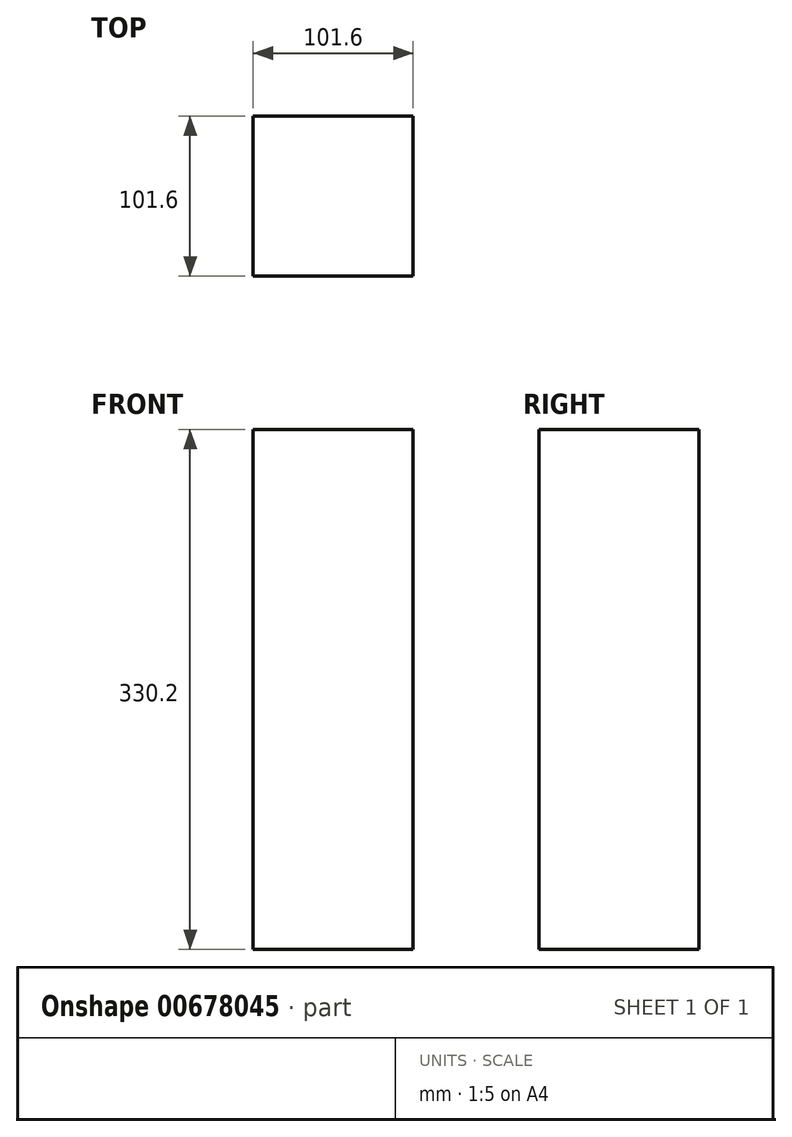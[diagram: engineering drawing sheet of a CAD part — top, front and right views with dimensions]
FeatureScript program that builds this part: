
annotation { "Feature Type Name" : "Feature", "Feature Type Description" : "" }
export const myFeature = defineFeature(function(context is Context, id is Id, definition is map)
    precondition{}
    {
        {
            var Q0;
            Q0=qCreatedBy(makeId("Top.planeOp"),FACE);
            var sketch = newSketch(context, id + "F0", { "sketchPlane" : qUnion([Q0])});
            skLineSegment(sketch, "E0.bottom", {"start": v(-50.8, 50.8) * mm, "end": v(50.8, 50.8) * mm});
            skLineSegment(sketch, "E0.top", {"start": v(-50.8, -50.8) * mm, "end": v(50.8, -50.8) * mm});
            skLineSegment(sketch, "E0.left", {"start": v(-50.8, 50.8) * mm, "end": v(-50.8, -50.8) * mm});
            skLineSegment(sketch, "E0.right", {"start": v(50.8, 50.8) * mm, "end": v(50.8, -50.8) * mm});
            skPoint(sketch, "E0.middle", {"position": v(0, 0) * mm});
            skSolve(sketch);
        }
        {
            var Q0;
            Q0 = qSketchRegion(id + "F0", true);
            extrude(context, id + "F1", {"entities" : qUnion([Q0]), "depth" : 330.2 * mm, "offsetDistance" : 25.4 * mm});
        }
        {
            var Q0;
            Q0=makeQuery(id+"F1.opExtrude","SWEPT_FACE",FACE,{"disambiguationData":[OSD([sQuery(id+"F0.wireOp",EDGE,"E0.top")])]});
            var sketch = newSketch(context, id + "F2", { "sketchPlane" : qUnion([Q0])});
            skSolve(sketch);
        }
    });
